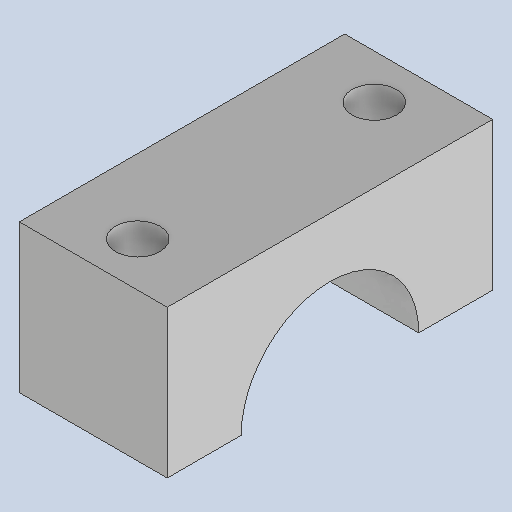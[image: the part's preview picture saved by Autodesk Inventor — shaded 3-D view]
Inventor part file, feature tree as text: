
AUTODESK INVENTOR PART (.ipt)
format: ipt  version: 2025.1 (Build 291241000, 241)  size: 109,568 bytes
history: native  units: mm
features: reference x6, other x3, extrude x2, sketch x2
ambient origin geometry x8: Origin, YZ Plane, XZ Plane, XY Plane, X Axis, Y Axis, Z Axis, Center Point
bodies: Solid1 (feature_tree)
feature tree (13):
  extrude  "Extrusion1"  Depth=10.0mm
  extrude  "Extrusion2"  [1 undecoded]
  sketch  "Sketch1"  dims[d0=10.0mm d1=0.0mm d2=12.0mm]
  reference  "Reference1"
  reference  "Reference2"
  reference  "Reference3"
  reference  "Reference4"
  reference  "Reference5"
  reference  "Reference6"
  sketch  "Sketch2"  dims[d3=10.0mm d4=0.0mm]
  parser-record x1  (decoder bookkeeping rows leaked as tree rows — omitted from the tree; the rows remain in map.json)
  other  "145.iam"
  other  "145 part 2:1"
note: 1 required parameter value undecoded (feature->parameter linkage not recoverable at this tier; creation-order binding heuristic only, values carry confidence <= 0.55)
note: 1 file-system path scrubbed to <path> (originals preserved in map.json)
